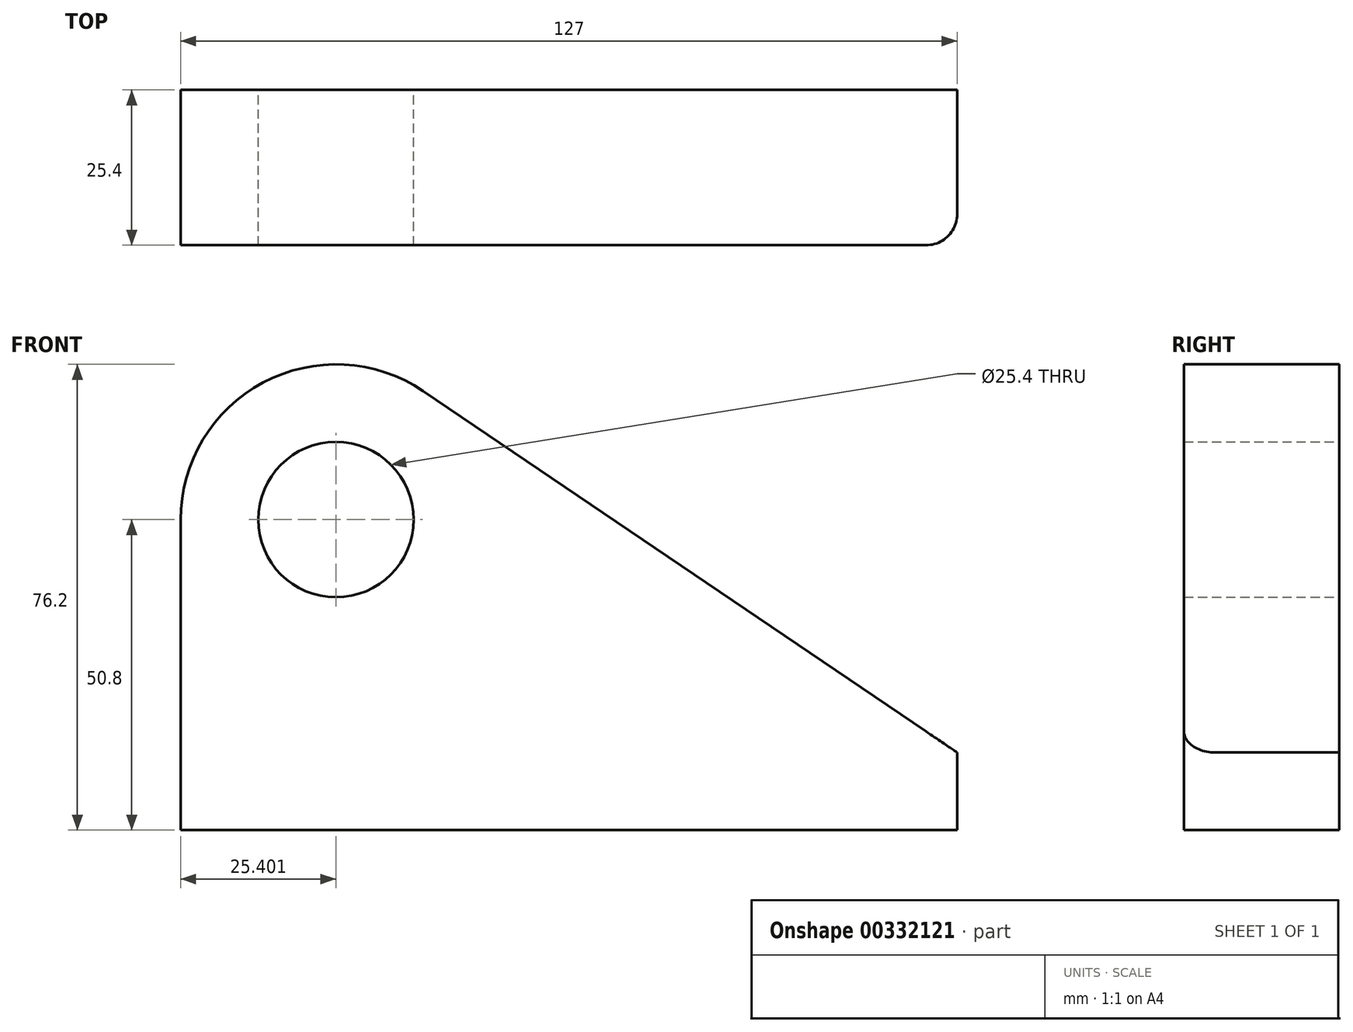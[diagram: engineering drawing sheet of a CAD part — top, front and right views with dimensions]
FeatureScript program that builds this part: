
annotation { "Feature Type Name" : "Feature", "Feature Type Description" : "" }
export const myFeature = defineFeature(function(context is Context, id is Id, definition is map)
    precondition{}
    {
        {
            var Q0;
            Q0=qCreatedBy(makeId("Front.planeOp"),FACE);
            var sketch = newSketch(context, id + "F0", { "sketchPlane" : qUnion([Q0])});
            skCircle(sketch, "E0", {"center": v(-47.55, 50.8) * mm, "radius": 12.7 * mm});
            skArc(sketch, "E1", {"start": v(-33.31, 71.83) * mm, "mid": v(-59.46, 73.24) * mm, "end": v(-72.95, 50.8) * mm});
            skLineSegment(sketch, "E2", {"start": v(-72.95, 50.8) * mm, "end": v(-72.95, 0) * mm});
            skLineSegment(sketch, "E3", {"start": v(-72.95, 0) * mm, "end": v(54.05, 0) * mm});
            skLineSegment(sketch, "E4", {"start": v(54.05, 0) * mm, "end": v(54.05, 12.7) * mm});
            skLineSegment(sketch, "E5", {"start": v(54.05, 12.7) * mm, "end": v(-33.31, 71.83) * mm});
            skSolve(sketch);
        }
        {
            var Q0;
            Q0=makeQuery(id+"F0.imprint","IMPRINT",FACE,{"disambiguationData":[TD([[makeQuery(id+"F0.imprint","IMPRINT",EDGE,{"derivedFrom":sQuery(id+"F0.wireOp",EDGE,"E0")}),-1.0]])]});
            extrude(context, id + "F1", {"entities" : qUnion([Q0]), "depth" : 25.4 * mm});
        }
        {
            var Q0;
            Q0=makeQuery(id+"F1.opExtrude","CAP_EDGE",EDGE,{"disambiguationData":[OSD([sQuery(id+"F0.wireOp",EDGE,"E4")])],"isStart":false});
            fillet(context, id + "F2", {"entities" : qUnion([Q0]), "radius" : 5.08 * mm, "tangentPropagation" : true, "allowEdgeOverflow" : false});
        }
    });
